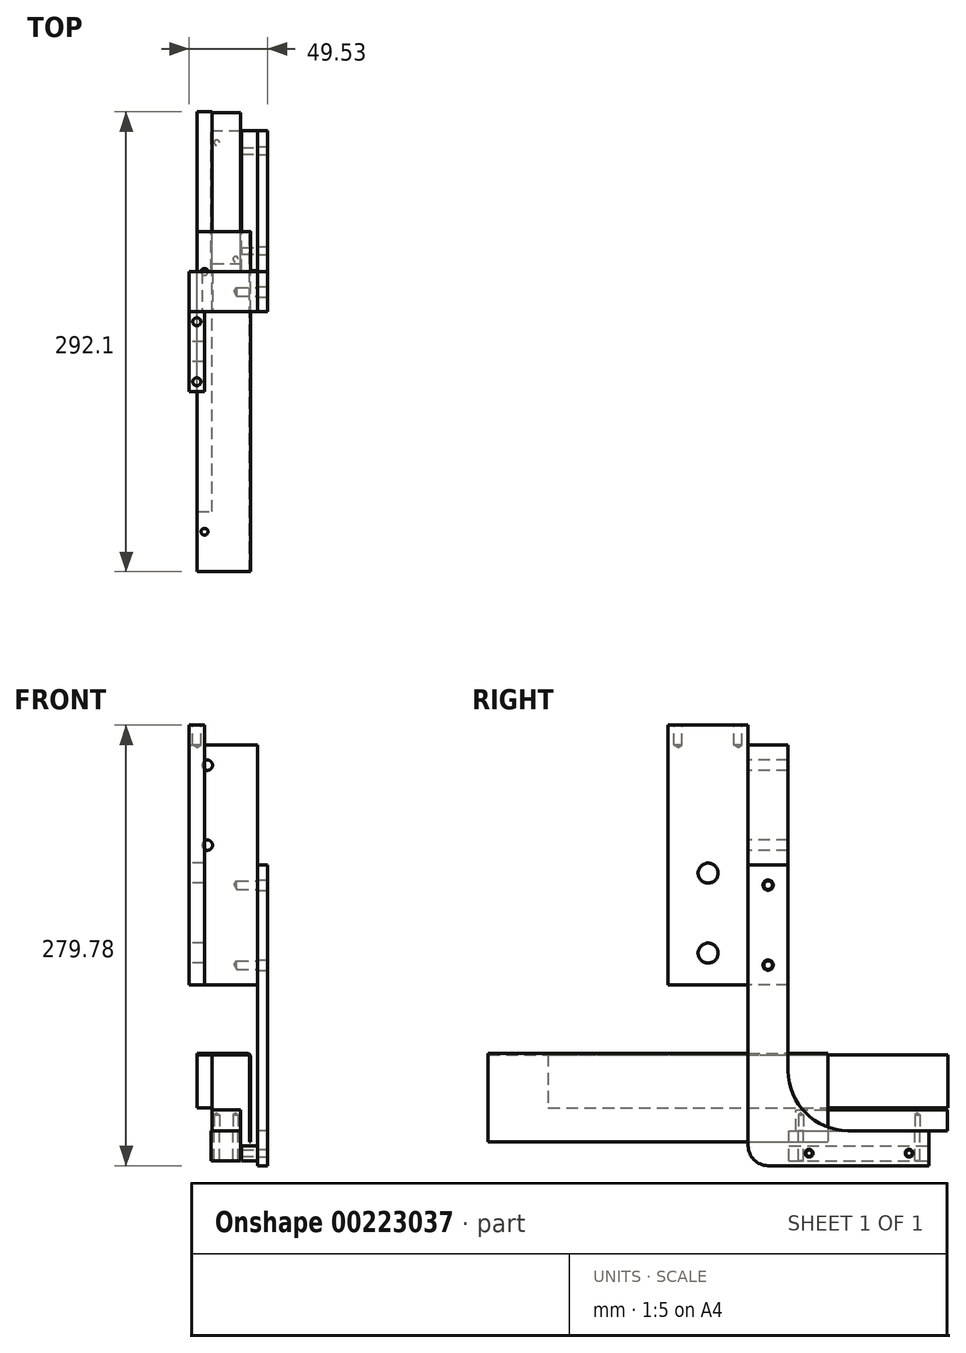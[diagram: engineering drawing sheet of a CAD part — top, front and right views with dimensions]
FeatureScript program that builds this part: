
annotation { "Feature Type Name" : "Feature", "Feature Type Description" : "" }
export const myFeature = defineFeature(function(context is Context, id is Id, definition is map)
    precondition{}
    {
        {
            var Q0;
            Q0=qCreatedBy(makeId("Front.planeOp"),FACE);
            var sketch = newSketch(context, id + "F0", { "sketchPlane" : qUnion([Q0])});
            skLineSegment(sketch, "E0.bottom", {"start": v(0, 0) * mm, "end": v(43.18, 0) * mm});
            skLineSegment(sketch, "E0.top", {"start": v(0, 152.4) * mm, "end": v(43.18, 152.4) * mm});
            skLineSegment(sketch, "E0.left", {"start": v(0, 0) * mm, "end": v(0, 152.4) * mm});
            skLineSegment(sketch, "E0.right", {"start": v(43.18, 0) * mm, "end": v(43.18, 152.4) * mm});
            skPoint(sketch, "E1", {"position": v(11.43, 139.7) * mm});
            skPoint(sketch, "E2", {"position": v(11.43, 88.9) * mm});
            skSolve(sketch);
        }
        {
            var Q0;
            Q0=makeQuery(id+"F0.imprint","IMPRINT",FACE,{"disambiguationData":[TD([[makeQuery(id+"F0.imprint","IMPRINT",EDGE,{"derivedFrom":sQuery(id+"F0.wireOp",EDGE,"E0.bottom")}),1.0]])]});
            extrude(context, id + "F1", {"entities" : qUnion([Q0]), "oppositeDirection" : true, "depth" : 25.4 * mm});
        }
        {
            var Q0;
            Q0=sQuery(id+"F0.wireOp",VERTEX,"E1");
            var Q1;
            Q1=sQuery(id+"F0.wireOp",VERTEX,"E2");
            var Q2;
            Q2=makeQuery(id+"F1.opExtrude","SWEPT_BODY",BODY,{"disambiguationData":[OSD([sQuery(id+"F0.wireOp",EDGE,"E0.bottom"),sQuery(id+"F0.wireOp",EDGE,"E0.top"),sQuery(id+"F0.wireOp",EDGE,"E0.left"),sQuery(id+"F0.wireOp",EDGE,"E0.right")])]});
            hole(context, id + "F2", {"style" : HoleStyle.SIMPLE, "endStyle" : HoleEndStyle.THROUGH, "standardTappedOrClearance" : lookupTablePath({ "standard" : "ANSI", "fit" : "Close", "size" : "1/4", "type" : "Clearance" }), "standardBlindInLast" : lookupTablePath({ "fit" : "Close", "standard" : "ANSI", "size" : "1/4", "type" : "Clearance" }), "holeDiameter" : 6.53 * mm, "locations" : qUnion([Q0, Q1]), "scope" : qUnion([Q2]), "isTappedThrough" : true});
        }
        {
            var Q0;
            Q0=qCreatedBy(makeId("Right.planeOp"),FACE);
            var sketch = newSketch(context, id + "F3", { "sketchPlane" : qUnion([Q0])});
            skLineSegment(sketch, "E3.bottom", {"start": v(0, 0) * mm, "end": v(-50.8, 0) * mm});
            skLineSegment(sketch, "E3.top", {"start": v(0, 165.1) * mm, "end": v(-50.8, 165.1) * mm});
            skLineSegment(sketch, "E3.left", {"start": v(0, 0) * mm, "end": v(0, 165.1) * mm});
            skLineSegment(sketch, "E3.right", {"start": v(-50.8, 0) * mm, "end": v(-50.8, 165.1) * mm});
            skPoint(sketch, "E4", {"position": v(-25.4, 71.12) * mm});
            skPoint(sketch, "E5", {"position": v(-25.4, 20.32) * mm});
            skSolve(sketch);
        }
        {
            var Q0;
            Q0=makeQuery(id+"F3.imprint","IMPRINT",FACE,{"disambiguationData":[TD([[makeQuery(id+"F3.imprint","IMPRINT",EDGE,{"derivedFrom":sQuery(id+"F3.wireOp",EDGE,"E3.bottom")}),-1.0]])]});
            extrude(context, id + "F4", {"entities" : qUnion([Q0]), "depth" : 9.52 * mm});
        }
        {
            var Q0;
            Q0=sQuery(id+"F3.wireOp",VERTEX,"E4");
            var Q1;
            Q1=sQuery(id+"F3.wireOp",VERTEX,"E5");
            var Q2;
            Q2=makeQuery(id+"F4.opExtrude","SWEPT_BODY",BODY,{"disambiguationData":[OSD([sQuery(id+"F3.wireOp",EDGE,"E3.bottom"),sQuery(id+"F3.wireOp",EDGE,"E3.top"),sQuery(id+"F3.wireOp",EDGE,"E3.left"),sQuery(id+"F3.wireOp",EDGE,"E3.right")])]});
            hole(context, id + "F5", {"style" : HoleStyle.SIMPLE, "endStyle" : HoleEndStyle.THROUGH, "oppositeDirection" : true, "holeDiameter" : 12.7 * mm, "locations" : qUnion([Q0, Q1]), "scope" : qUnion([Q2]), "isTappedThrough" : true});
        }
        {
            var Q0;
            Q0=makeQuery(id+"F4.opExtrude","SWEPT_FACE",FACE,{"disambiguationData":[OSD([sQuery(id+"F3.wireOp",EDGE,"E3.top")])]});
            var sketch = newSketch(context, id + "F6", { "sketchPlane" : qUnion([Q0])});
            skPoint(sketch, "E6", {"position": v(4.76, -6.35) * mm});
            skPoint(sketch, "E6.positionSnap0", {"position": v(4.76, 0) * mm});
            skPoint(sketch, "E7", {"position": v(4.76, -44.45) * mm});
            skSolve(sketch);
        }
        {
            var Q0;
            Q0=sQuery(id+"F6.wireOp",VERTEX,"E6");
            var Q1;
            Q1=sQuery(id+"F6.wireOp",VERTEX,"E7");
            var Q2;
            Q2=makeQuery(id+"F4.opExtrude","SWEPT_BODY",BODY,{"disambiguationData":[OSD([sQuery(id+"F3.wireOp",EDGE,"E3.bottom"),sQuery(id+"F3.wireOp",EDGE,"E3.top"),sQuery(id+"F3.wireOp",EDGE,"E3.left"),sQuery(id+"F3.wireOp",EDGE,"E3.right")])]});
            hole(context, id + "F7", {"style" : HoleStyle.SIMPLE, "endStyle" : HoleEndStyle.BLIND, "standardTappedOrClearance" : lookupTablePath({ "standard" : "ANSI", "engagement" : "75%", "pitch" : "20 tpi", "size" : "1/4", "type" : "Tapped" }), "standardBlindInLast" : lookupTablePath({ "standard" : "ANSI", "engagement" : "75%", "pitch" : "20 tpi", "size" : "1/4", "type" : "Tapped" }), "holeDiameter" : 5.1 * mm, "holeDepth" : 12.7 * mm, "locations" : qUnion([Q0, Q1]), "scope" : qUnion([Q2]), "majorDiameter" : 6.35 * mm});
        }
        {
            var Q0;
            Q0=qCreatedBy(makeId("Front.planeOp"),FACE);
            var sketch = newSketch(context, id + "F8", { "sketchPlane" : qUnion([Q0])});
            skLineSegment(sketch, "E8.bottom", {"start": v(4.9, -44.22) * mm, "end": v(14.43, -44.22) * mm});
            skLineSegment(sketch, "E8.top", {"start": v(4.9, -78.1) * mm, "end": v(14.43, -78.1) * mm});
            skLineSegment(sketch, "E8.left", {"start": v(4.9, -44.22) * mm, "end": v(4.9, -78.1) * mm});
            skLineSegment(sketch, "E8.right", {"start": v(14.43, -44.22) * mm, "end": v(14.43, -78.1) * mm});
            skSolve(sketch);
        }
        {
            var Q0;
            Q0=makeQuery(id+"F8.imprint","IMPRINT",FACE,{"disambiguationData":[TD([[makeQuery(id+"F8.imprint","IMPRINT",EDGE,{"derivedFrom":sQuery(id+"F8.wireOp",EDGE,"E8.bottom")}),-1.0]])]});
            extrude(context, id + "F9", {"entities" : qUnion([Q0]), "endBound" : BoundingType.SYMMETRIC, "depth" : 254 * mm});
        }
        {
            var Q0;
            Q0=makeQuery(id+"F9.opExtrude","SWEPT_FACE",FACE,{"disambiguationData":[OSD([sQuery(id+"F8.wireOp",EDGE,"E8.top")])]});
            cPlane(context, id + "F10", {"entities" : qUnion([Q0]), "cplaneType" : CPlaneType.OFFSET, "offset" : 1.02 * mm, "width" : 152.4 * mm, "height" : 152.4 * mm});
        }
        {
            var Q0;
            Q0=qCreatedBy(id+"F10.planeOp",FACE);
            var sketch = newSketch(context, id + "F11", { "sketchPlane" : qUnion([Q0])});
            skLineSegment(sketch, "E9.0", {"start": v(14.43, 127) * mm, "end": v(14.43, -127) * mm});
            skLineSegment(sketch, "E10.bottom", {"start": v(14.43, -30.48) * mm, "end": v(32.44, -30.48) * mm});
            skLineSegment(sketch, "E10.top", {"start": v(14.43, -126.48) * mm, "end": v(32.44, -126.48) * mm});
            skLineSegment(sketch, "E10.left", {"start": v(14.43, -30.48) * mm, "end": v(14.43, -126.48) * mm});
            skLineSegment(sketch, "E10.right", {"start": v(32.44, -30.48) * mm, "end": v(32.44, -126.48) * mm});
            skPoint(sketch, "E11", {"position": v(29.44, -33.48) * mm});
            skPoint(sketch, "E12", {"position": v(17.44, -107.48) * mm});
            skSolve(sketch);
        }
        {
            var Q0;
            Q0=makeQuery(id+"F11.imprint","IMPRINT",FACE,{"disambiguationData":[TD([[makeQuery(id+"F11.imprint","IMPRINT",EDGE,{"derivedFrom":sQuery(id+"F11.wireOp",EDGE,"E10.bottom")}),-1.0]])]});
            extrude(context, id + "F12", {"entities" : qUnion([Q0]), "depth" : 13.33 * mm});
        }
        {
            var Q0;
            Q0=makeQuery(id+"F12.opExtrude","CAP_FACE",FACE,{"disambiguationData":[OSD([sQuery(id+"F11.wireOp",EDGE,"E10.bottom"),sQuery(id+"F11.wireOp",EDGE,"E10.top"),sQuery(id+"F11.wireOp",EDGE,"E10.left"),sQuery(id+"F11.wireOp",EDGE,"E10.right")])],"isStart":false});
            var sketch = newSketch(context, id + "F13", { "sketchPlane" : qUnion([Q0])});
            skLineSegment(sketch, "E13.0.0", {"start": v(32.44, -30.48) * mm, "end": v(14.43, -30.48) * mm});
            skLineSegment(sketch, "E13.0.1", {"start": v(14.43, -30.48) * mm, "end": v(14.43, -126.48) * mm});
            skLineSegment(sketch, "E13.0.2", {"start": v(14.43, -126.48) * mm, "end": v(32.44, -126.48) * mm});
            skLineSegment(sketch, "E13.0.3", {"start": v(32.44, -126.48) * mm, "end": v(32.44, -30.48) * mm});
            skPoint(sketch, "E14.0", {"position": v(29.44, -33.48) * mm});
            skPoint(sketch, "E15.0", {"position": v(17.44, -107.48) * mm});
            skSolve(sketch);
        }
        {
            var Q0;
            Q0=sQuery(id+"F13.wireOp",VERTEX,"E14.0");
            var Q1;
            Q1=sQuery(id+"F13.wireOp",VERTEX,"E15.0");
            var Q2;
            Q2=makeQuery(id+"F12.opExtrude","SWEPT_BODY",BODY,{"disambiguationData":[OSD([sQuery(id+"F11.wireOp",EDGE,"E10.bottom"),sQuery(id+"F11.wireOp",EDGE,"E10.top"),sQuery(id+"F11.wireOp",EDGE,"E10.left"),sQuery(id+"F11.wireOp",EDGE,"E10.right")])]});
            hole(context, id + "F14", {"style" : HoleStyle.SIMPLE, "endStyle" : HoleEndStyle.BLIND, "standardTappedOrClearance" : lookupTablePath({ "standard" : "ISO", "engagement" : "75%", "pitch" : "0.7 mm", "size" : "M4", "type" : "Tapped" }), "standardBlindInLast" : lookupTablePath({ "standard" : "ISO", "engagement" : "75%", "pitch" : "0.7 mm", "size" : "M4", "type" : "Tapped" }), "holeDiameter" : 3.3 * mm, "showTappedDepth" : true, "holeDepth" : 10.16 * mm, "tappedDepth" : 8.06 * mm, "tapClearance" : 3, "locations" : qUnion([Q0, Q1]), "scope" : qUnion([Q2]), "majorDiameter" : 4 * mm});
        }
        {
            var Q0;
            Q0=makeQuery(id+"F12.opExtrude","CAP_FACE",FACE,{"disambiguationData":[OSD([sQuery(id+"F11.wireOp",EDGE,"E10.bottom"),sQuery(id+"F11.wireOp",EDGE,"E10.top"),sQuery(id+"F11.wireOp",EDGE,"E10.left"),sQuery(id+"F11.wireOp",EDGE,"E10.right")])],"isStart":false});
            var sketch = newSketch(context, id + "F15", { "sketchPlane" : qUnion([Q0])});
            skLineSegment(sketch, "E16.bottom", {"start": v(14.43, -26.04) * mm, "end": v(43.18, -26.04) * mm});
            skLineSegment(sketch, "E16.top", {"start": v(14.43, -114.94) * mm, "end": v(43.18, -114.94) * mm});
            skLineSegment(sketch, "E16.left", {"start": v(14.43, -26.04) * mm, "end": v(14.43, -114.94) * mm});
            skLineSegment(sketch, "E16.right", {"start": v(43.18, -26.04) * mm, "end": v(43.18, -114.94) * mm});
            skLineSegment(sketch, "E17", {"start": v(32.44, -30.48) * mm, "end": v(32.44, -26.04) * mm});
            skLineSegment(sketch, "E18.bottom", {"start": v(14.43, -26.04) * mm, "end": v(13.67, -26.04) * mm});
            skLineSegment(sketch, "E18.top", {"start": v(14.43, -114.94) * mm, "end": v(13.67, -114.94) * mm});
            skLineSegment(sketch, "E18.right", {"start": v(13.67, -26.04) * mm, "end": v(13.67, -114.94) * mm});
            skLineSegment(sketch, "E19.bottom", {"start": v(32.44, -26.04) * mm, "end": v(33.2, -26.04) * mm});
            skLineSegment(sketch, "E19.top", {"start": v(32.44, -114.94) * mm, "end": v(33.2, -114.94) * mm});
            skLineSegment(sketch, "E19.left", {"start": v(32.44, -26.04) * mm, "end": v(32.44, -114.94) * mm});
            skLineSegment(sketch, "E19.right", {"start": v(33.2, -26.04) * mm, "end": v(33.2, -114.94) * mm});
            skSolve(sketch);
        }
        {
            var Q0;
            {var subQ0=makeQuery(id+"F12.opExtrude","CAP_EDGE",EDGE,{"disambiguationData":[OSD([sQuery(id+"F11.wireOp",EDGE,"E10.bottom")])],"isStart":false});Q0=makeQuery(id+"F15.imprint","IMPRINT",FACE,{"disambiguationData":[TD([[makeQuery(id+"F15.imprint","IMPRINT",EDGE,{"derivedFrom":subQ0}),-1.0]])]});}
            var Q1;
            {var subQ3=sQuery(id+"F15.wireOp",EDGE,"E17");Q1=makeQuery(id+"F15.imprint","IMPRINT",FACE,{"disambiguationData":[TD([[makeQuery(id+"F15.imprint","IMPRINT",EDGE,{"derivedFrom":subQ3}),1.0]])]});}
            var Q2;
            Q2=makeQuery(id+"F15.imprint","IMPRINT",FACE,{"disambiguationData":[TD([[makeQuery(id+"F15.imprint","IMPRINT",EDGE,{"derivedFrom":makeQuery(id+"F14.hole-0.boolean.opBoolean","COPY",EDGE,{"derivedFrom":makeQuery(id+"F14.hole-0.opRevolve","SWEPT_EDGE",EDGE,{"disambiguationData":[OSD([sQuery(id+"F14.hole-0.sketch.wireOp",EDGE,"core_line_2"),sQuery(id+"F14.hole-0.sketch.wireOp",EDGE,"core_line_3")])]})})}),1.0]])]});
            var Q3;
            Q3=makeQuery(id+"F15.imprint","IMPRINT",FACE,{"disambiguationData":[TD([[makeQuery(id+"F15.imprint","IMPRINT",EDGE,{"derivedFrom":makeQuery(id+"F14.hole-1.boolean.opBoolean","COPY",EDGE,{"derivedFrom":makeQuery(id+"F14.hole-1.opRevolve","SWEPT_EDGE",EDGE,{"disambiguationData":[OSD([sQuery(id+"F14.hole-1.sketch.wireOp",EDGE,"core_line_2"),sQuery(id+"F14.hole-1.sketch.wireOp",EDGE,"core_line_3")])]})})}),1.0]])]});
            var Q4;
            {var subQ1=sQuery(id+"F15.wireOp",EDGE,"E16.right");Q4=makeQuery(id+"F15.imprint","IMPRINT",FACE,{"disambiguationData":[TD([[makeQuery(id+"F15.imprint","IMPRINT",EDGE,{"derivedFrom":subQ1}),-1.0]])]});}
            var Q5;
            {var subQ2=sQuery(id+"F15.wireOp",EDGE,"E18.bottom");Q5=makeQuery(id+"F15.imprint","IMPRINT",FACE,{"disambiguationData":[TD([[makeQuery(id+"F15.imprint","IMPRINT",EDGE,{"derivedFrom":subQ2}),1.0]])]});}
            var Q6;
            {var subQ2=sQuery(id+"F15.wireOp",EDGE,"E19.bottom");Q6=makeQuery(id+"F15.imprint","IMPRINT",FACE,{"disambiguationData":[TD([[makeQuery(id+"F15.imprint","IMPRINT",EDGE,{"derivedFrom":subQ2}),-1.0]])]});}
            var Q7;
            {var subQ5=makeQuery(id+"F12.opExtrude","CAP_EDGE",EDGE,{"disambiguationData":[OSD([sQuery(id+"F11.wireOp",EDGE,"E10.bottom")])],"isStart":false});Q7=makeQuery(id+"F15.imprint","IMPRINT",FACE,{"disambiguationData":[TD([[makeQuery(id+"F15.imprint","IMPRINT",EDGE,{"derivedFrom":subQ5}),1.0]])]});}
            extrude(context, id + "F16", {"entities" : qUnion([Q0, Q1, Q2, Q3, Q4, Q5, Q6, Q7]), "depth" : 19.05 * mm});
        }
        {
            var Q0;
            {var subQ1=sQuery(id+"F15.wireOp",EDGE,"E16.right");Q0=makeQuery(id+"F15.imprint","IMPRINT",FACE,{"disambiguationData":[TD([[makeQuery(id+"F15.imprint","IMPRINT",EDGE,{"derivedFrom":subQ1}),-1.0]])]});}
            extrude(context, id + "F17", {"entities" : qUnion([Q0]), "operationType" : NewBodyOperationType.REMOVE, "depth" : 9.52 * mm});
        }
        {
            var Q0;
            Q0=sQuery(id+"F13.wireOp",VERTEX,"E14.0");
            var Q1;
            Q1=sQuery(id+"F13.wireOp",VERTEX,"E15.0");
            var Q2;
            Q2=makeQuery(id+"F16.opExtrude","SWEPT_BODY",BODY,{"disambiguationData":[OSD([sQuery(id+"F15.wireOp",EDGE,"E16.bottom"),sQuery(id+"F15.wireOp",EDGE,"E16.top"),sQuery(id+"F15.wireOp",EDGE,"E16.left"),sQuery(id+"F15.wireOp",EDGE,"E16.right")])]});
            hole(context, id + "F18", {"style" : HoleStyle.SIMPLE, "endStyle" : HoleEndStyle.THROUGH, "oppositeDirection" : true, "standardTappedOrClearance" : lookupTablePath({ "standard" : "ISO", "fit" : "Normal", "size" : "M4", "type" : "Clearance" }), "standardBlindInLast" : lookupTablePath({ "fit" : "Standard", "standard" : "ISO", "size" : "M4", "type" : "Clearance" }), "holeDiameter" : 4.4 * mm, "tappedDepth" : 8.06 * mm, "tapClearance" : 3, "locations" : qUnion([Q0, Q1]), "scope" : qUnion([Q2])});
        }
        {
            var Q0;
            Q0=makeQuery(id+"F16.opExtrude","SWEPT_FACE",FACE,{"disambiguationData":[OSD([sQuery(id+"F15.wireOp",EDGE,"E16.right")])]});
            var sketch = newSketch(context, id + "F19", { "sketchPlane" : qUnion([Q0])});
            skPoint(sketch, "E20", {"position": v(38.74, -106.74) * mm});
            skPoint(sketch, "E20.positionSnap0", {"position": v(26.04, -106.74) * mm});
            skPoint(sketch, "E21", {"position": v(102.23, -106.74) * mm});
            skSolve(sketch);
        }
        {
            var Q0;
            Q0=sQuery(id+"F19.wireOp",VERTEX,"E20");
            var Q1;
            Q1=sQuery(id+"F19.wireOp",VERTEX,"E21");
            var Q2;
            Q2=makeQuery(id+"F16.opExtrude","SWEPT_BODY",BODY,{"disambiguationData":[OSD([sQuery(id+"F15.wireOp",EDGE,"E16.bottom"),sQuery(id+"F15.wireOp",EDGE,"E16.top"),sQuery(id+"F15.wireOp",EDGE,"E16.right"),sQuery(id+"F15.wireOp",EDGE,"E18.bottom"),sQuery(id+"F15.wireOp",EDGE,"E18.top"),sQuery(id+"F15.wireOp",EDGE,"E18.right"),sQuery(id+"F15.wireOp",EDGE,"E19.bottom"),sQuery(id+"F15.wireOp",EDGE,"E19.top")])]});
            hole(context, id + "F20", {"style" : HoleStyle.SIMPLE, "endStyle" : HoleEndStyle.BLIND, "standardTappedOrClearance" : lookupTablePath({ "standard" : "ANSI", "engagement" : "75%", "pitch" : "32 tpi", "size" : "#10", "type" : "Tapped" }), "standardBlindInLast" : lookupTablePath({ "standard" : "ANSI", "engagement" : "75%", "pitch" : "32 tpi", "size" : "#10", "type" : "Tapped" }), "holeDiameter" : 4.04 * mm, "showTappedDepth" : true, "holeDepth" : 12.7 * mm, "tappedDepth" : 10.32 * mm, "tapClearance" : 3, "locations" : qUnion([Q0, Q1]), "scope" : qUnion([Q2]), "majorDiameter" : 4.83 * mm});
        }
        {
            var Q0;
            Q0=makeQuery(id+"F1.opExtrude","SWEPT_FACE",FACE,{"disambiguationData":[OSD([sQuery(id+"F0.wireOp",EDGE,"E0.right")])]});
            var sketch = newSketch(context, id + "F21", { "sketchPlane" : qUnion([Q0])});
            skPoint(sketch, "E22", {"position": v(12.7, 12.7) * mm});
            skPoint(sketch, "E22.positionSnap0", {"position": v(12.7, 0) * mm});
            skPoint(sketch, "E23", {"position": v(12.7, 63.5) * mm});
            skSolve(sketch);
        }
        {
            var Q0;
            Q0=sQuery(id+"F21.wireOp",VERTEX,"E23");
            var Q1;
            Q1=sQuery(id+"F21.wireOp",VERTEX,"E22");
            var Q2;
            Q2=makeQuery(id+"F1.opExtrude","SWEPT_BODY",BODY,{"disambiguationData":[OSD([sQuery(id+"F0.wireOp",EDGE,"E0.bottom"),sQuery(id+"F0.wireOp",EDGE,"E0.top"),sQuery(id+"F0.wireOp",EDGE,"E0.left"),sQuery(id+"F0.wireOp",EDGE,"E0.right")])]});
            hole(context, id + "F22", {"style" : HoleStyle.SIMPLE, "endStyle" : HoleEndStyle.BLIND, "standardTappedOrClearance" : lookupTablePath({ "standard" : "ANSI", "engagement" : "75%", "pitch" : "28 tpi", "size" : "1/4", "type" : "Tapped" }), "standardBlindInLast" : lookupTablePath({ "standard" : "ANSI", "engagement" : "75%", "pitch" : "28 tpi", "size" : "1/4", "type" : "Tapped" }), "holeDiameter" : 5.4 * mm, "showTappedDepth" : true, "holeDepth" : 13.04 * mm, "tappedDepth" : 10.32 * mm, "tapClearance" : 3, "locations" : qUnion([Q0, Q1]), "scope" : qUnion([Q2]), "majorDiameter" : 6.35 * mm});
        }
        {
            var Q0;
            Q0=makeQuery(id+"F1.opExtrude","SWEPT_FACE",FACE,{"disambiguationData":[OSD([sQuery(id+"F0.wireOp",EDGE,"E0.right")])]});
            var sketch = newSketch(context, id + "F23", { "sketchPlane" : qUnion([Q0])});
            skLineSegment(sketch, "E24.0.0", {"start": v(114.94, -101.98) * mm, "end": v(26.04, -101.98) * mm});
            skLineSegment(sketch, "E24.0.1", {"start": v(26.04, -101.98) * mm, "end": v(26.04, -111.5) * mm});
            skLineSegment(sketch, "E24.0.2", {"start": v(26.04, -111.5) * mm, "end": v(114.94, -111.5) * mm});
            skLineSegment(sketch, "E24.0.3", {"start": v(114.94, -111.5) * mm, "end": v(114.94, -101.98) * mm});
            skLineSegment(sketch, "E25.bottom", {"start": v(0, 76.2) * mm, "end": v(25.4, 76.2) * mm});
            skLineSegment(sketch, "E25.top", {"start": v(0, -111.5) * mm, "end": v(114.94, -111.5) * mm});
            skLineSegment(sketch, "E25.left", {"start": v(0, 76.2) * mm, "end": v(0, -111.5) * mm});
            skLineSegment(sketch, "E25.right", {"start": v(114.94, -101.98) * mm, "end": v(114.94, -111.5) * mm});
            skLineSegment(sketch, "E26", {"start": v(25.4, 76.2) * mm, "end": v(25.4, -101.98) * mm});
            skLineSegment(sketch, "E27", {"start": v(25.4, -101.98) * mm, "end": v(114.94, -101.98) * mm});
            skCircle(sketch, "E28", {"center": v(63.5, -54.36) * mm, "radius": 38.1 * mm});
            skLineSegment(sketch, "E29", {"start": v(114.94, -101.98) * mm, "end": v(114.94, -92.46) * mm});
            skLineSegment(sketch, "E30", {"start": v(114.94, -92.46) * mm, "end": v(25.4, -92.46) * mm});
            skLineSegment(sketch, "E31.top", {"start": v(0, -114.68) * mm, "end": v(114.94, -114.68) * mm});
            skLineSegment(sketch, "E31.left", {"start": v(0, -111.5) * mm, "end": v(0, -114.68) * mm});
            skLineSegment(sketch, "E31.right", {"start": v(114.94, -111.5) * mm, "end": v(114.94, -114.68) * mm});
            skSolve(sketch);
        }
        {
            var Q0;
            {var subQ3=sQuery(id+"F23.wireOp",EDGE,"E25.bottom");Q0=makeQuery(id+"F23.imprint","IMPRINT",FACE,{"disambiguationData":[TD([[makeQuery(id+"F23.imprint","IMPRINT",EDGE,{"derivedFrom":subQ3}),-1.0]])]});}
            var Q1;
            {var subQ6=sQuery(id+"F23.wireOp",EDGE,"E24.0.1");Q1=makeQuery(id+"F23.imprint","IMPRINT",FACE,{"disambiguationData":[TD([[makeQuery(id+"F23.imprint","IMPRINT",EDGE,{"derivedFrom":subQ6}),-1.0]])]});}
            var Q2;
            {var subQ2=sQuery(id+"F23.wireOp",EDGE,"E29");Q2=makeQuery(id+"F23.imprint","IMPRINT",FACE,{"disambiguationData":[TD([[makeQuery(id+"F23.imprint","IMPRINT",EDGE,{"derivedFrom":subQ2}),1.0]])]});}
            var Q3;
            {var subQ0=sQuery(id+"F23.wireOp",EDGE,"E24.0.1");Q3=makeQuery(id+"F23.imprint","IMPRINT",FACE,{"disambiguationData":[TD([[makeQuery(id+"F23.imprint","IMPRINT",EDGE,{"derivedFrom":subQ0}),1.0]])]});}
            var Q4;
            {var subQ0=sQuery(id+"F23.wireOp",EDGE,"E30");var subQ1=sQuery(id+"F23.wireOp",EDGE,"E26");var subQ2=makeQuery(id+"F23.imprint","INTERSECT",VERTEX,{"derivedFrom":[subQ1,subQ0]});Q4=makeQuery(id+"F23.imprint","IMPRINT",FACE,{"disambiguationData":[TD([[makeQuery(id+"F23.imprint","IMPRINT",EDGE,{"disambiguationData":[TD([[subQ2,1.0]])],"derivedFrom":subQ1}),1.0]])]});}
            var Q5;
            Q5=makeQuery(id+"F23.imprint","IMPRINT",FACE,{"disambiguationData":[TD([[makeQuery(id+"F23.imprint","IMPRINT",EDGE,{"derivedFrom":makeQuery(id+"F22.hole-0.boolean.opBoolean","COPY",EDGE,{"derivedFrom":makeQuery(id+"F22.hole-0.opRevolve","SWEPT_EDGE",EDGE,{"disambiguationData":[OSD([sQuery(id+"F22.hole-0.sketch.wireOp",EDGE,"core_line_2"),sQuery(id+"F22.hole-0.sketch.wireOp",EDGE,"core_line_3")])]})})}),1.0]])]});
            var Q6;
            Q6=makeQuery(id+"F23.imprint","IMPRINT",FACE,{"disambiguationData":[TD([[makeQuery(id+"F23.imprint","IMPRINT",EDGE,{"derivedFrom":makeQuery(id+"F22.hole-1.boolean.opBoolean","COPY",EDGE,{"derivedFrom":makeQuery(id+"F22.hole-1.opRevolve","SWEPT_EDGE",EDGE,{"disambiguationData":[OSD([sQuery(id+"F22.hole-1.sketch.wireOp",EDGE,"core_line_2"),sQuery(id+"F22.hole-1.sketch.wireOp",EDGE,"core_line_3")])]})})}),1.0]])]});
            var Q7;
            Q7=makeQuery(id+"F23.imprint","IMPRINT",FACE,{"disambiguationData":[TD([[makeQuery(id+"F23.imprint","IMPRINT",EDGE,{"derivedFrom":sQuery(id+"F23.wireOp",EDGE,"E31.top")}),1.0]])]});
            extrude(context, id + "F24", {"entities" : qUnion([Q0, Q1, Q2, Q3, Q4, Q5, Q6, Q7]), "depth" : 6.35 * mm});
        }
        {
            var Q0;
            Q0=makeQuery(id+"F24.opExtrude","CAP_FACE",FACE,{"disambiguationData":[OSD([sQuery(id+"F23.wireOp",EDGE,"E25.bottom"),sQuery(id+"F23.wireOp",EDGE,"E25.top"),sQuery(id+"F23.wireOp",EDGE,"E25.left"),sQuery(id+"F23.wireOp",EDGE,"E25.right"),sQuery(id+"F23.wireOp",EDGE,"E26"),sQuery(id+"F23.wireOp",EDGE,"E28"),sQuery(id+"F23.wireOp",EDGE,"E29"),sQuery(id+"F23.wireOp",EDGE,"E30")])],"isStart":false});
            var sketch = newSketch(context, id + "F25", { "sketchPlane" : qUnion([Q0])});
            skLineSegment(sketch, "E32.0.0", {"start": v(0, 152.4) * mm, "end": v(0, 0) * mm});
            skLineSegment(sketch, "E32.0.1", {"start": v(0, 0) * mm, "end": v(25.4, 0) * mm});
            skLineSegment(sketch, "E32.0.2", {"start": v(25.4, 0) * mm, "end": v(25.4, 152.4) * mm});
            skLineSegment(sketch, "E32.0.3", {"start": v(25.4, 152.4) * mm, "end": v(0, 152.4) * mm});
            skCircle(sketch, "E33.0", {"center": v(102.23, -106.74) * mm, "radius": 2.02 * mm});
            skCircle(sketch, "E34.0", {"center": v(38.74, -106.74) * mm, "radius": 2.02 * mm});
            skCircle(sketch, "E35.0", {"center": v(12.7, 12.7) * mm, "radius": 2.7 * mm});
            skCircle(sketch, "E36.0", {"center": v(12.7, 63.5) * mm, "radius": 2.7 * mm});
            skSolve(sketch);
        }
        {
            var Q0;
            Q0=sQuery(id+"F25.wireOp",VERTEX,"E36.0.center");
            var Q1;
            Q1=sQuery(id+"F25.wireOp",VERTEX,"E35.0.center");
            var Q2;
            Q2=makeQuery(id+"F24.opExtrude","SWEPT_BODY",BODY,{"disambiguationData":[OSD([sQuery(id+"F23.wireOp",EDGE,"E25.bottom"),sQuery(id+"F23.wireOp",EDGE,"E25.top"),sQuery(id+"F23.wireOp",EDGE,"E25.left"),sQuery(id+"F23.wireOp",EDGE,"E25.right"),sQuery(id+"F23.wireOp",EDGE,"E26"),sQuery(id+"F23.wireOp",EDGE,"E28"),sQuery(id+"F23.wireOp",EDGE,"E29"),sQuery(id+"F23.wireOp",EDGE,"E30")])]});
            hole(context, id + "F26", {"style" : HoleStyle.SIMPLE, "endStyle" : HoleEndStyle.THROUGH, "standardTappedOrClearance" : lookupTablePath({ "standard" : "ANSI", "fit" : "Close", "size" : "1/4", "type" : "Clearance" }), "standardBlindInLast" : lookupTablePath({ "fit" : "Close", "standard" : "ANSI", "size" : "1/4", "type" : "Clearance" }), "holeDiameter" : 6.53 * mm, "tappedDepth" : 10.3 * mm, "tapClearance" : 3, "locations" : qUnion([Q0, Q1]), "scope" : qUnion([Q2])});
        }
        {
            var Q0;
            Q0=sQuery(id+"F25.wireOp",VERTEX,"E34.0.center");
            var Q1;
            Q1=sQuery(id+"F25.wireOp",VERTEX,"E33.0.center");
            var Q2;
            Q2=makeQuery(id+"F24.opExtrude","SWEPT_BODY",BODY,{"disambiguationData":[OSD([sQuery(id+"F23.wireOp",EDGE,"E25.bottom"),sQuery(id+"F23.wireOp",EDGE,"E25.top"),sQuery(id+"F23.wireOp",EDGE,"E25.left"),sQuery(id+"F23.wireOp",EDGE,"E25.right"),sQuery(id+"F23.wireOp",EDGE,"E26"),sQuery(id+"F23.wireOp",EDGE,"E28"),sQuery(id+"F23.wireOp",EDGE,"E29"),sQuery(id+"F23.wireOp",EDGE,"E30")])]});
            hole(context, id + "F27", {"style" : HoleStyle.SIMPLE, "endStyle" : HoleEndStyle.THROUGH, "standardTappedOrClearance" : lookupTablePath({ "standard" : "ANSI", "fit" : "Close", "size" : "#10", "type" : "Clearance" }), "standardBlindInLast" : lookupTablePath({ "fit" : "Close", "standard" : "ANSI", "size" : "#10", "type" : "Clearance" }), "holeDiameter" : 4.98 * mm, "tappedDepth" : 10.3 * mm, "tapClearance" : 3, "locations" : qUnion([Q0, Q1]), "scope" : qUnion([Q2])});
        }
        {
            var Q0;
            Q0=makeQuery(id+"F24.opExtrude","SWEPT_EDGE",EDGE,{"disambiguationData":[OSD([sQuery(id+"F23.wireOp",EDGE,"E31.top"),sQuery(id+"F23.wireOp",EDGE,"E31.left")])]});
            fillet(context, id + "F28", {"entities" : qUnion([Q0]), "radius" : 12.7 * mm, "tangentPropagation" : true, "allowEdgeOverflow" : false});
        }
        {
            var Q0;
            Q0=qCreatedBy(makeId("Front.planeOp"),FACE);
            cPlane(context, id + "F29", {"entities" : qUnion([Q0]), "cplaneType" : CPlaneType.OFFSET, "offset" : 50.8 * mm, "oppositeDirection" : true, "width" : 152.4 * mm, "height" : 152.4 * mm});
        }
        {
            var Q0;
            Q0=qCreatedBy(id+"F29.planeOp",FACE);
            var sketch = newSketch(context, id + "F30", { "sketchPlane" : qUnion([Q0])});
            skLineSegment(sketch, "E37.0.0", {"start": v(4.9, -78.1) * mm, "end": v(4.9, -44.22) * mm});
            skLineSegment(sketch, "E37.0.1", {"start": v(4.9, -44.22) * mm, "end": v(14.43, -44.22) * mm});
            skLineSegment(sketch, "E37.0.2", {"start": v(14.43, -44.22) * mm, "end": v(14.43, -78.1) * mm});
            skLineSegment(sketch, "E37.0.3", {"start": v(14.43, -78.1) * mm, "end": v(4.9, -78.1) * mm});
            skLineSegment(sketch, "E38.0.0", {"start": v(33.2, -92.46) * mm, "end": v(33.2, -101.98) * mm});
            skLineSegment(sketch, "E38.0.1", {"start": v(33.2, -101.98) * mm, "end": v(43.18, -101.98) * mm});
            skLineSegment(sketch, "E38.0.2", {"start": v(43.18, -101.98) * mm, "end": v(43.18, -111.5) * mm});
            skLineSegment(sketch, "E38.0.3", {"start": v(43.18, -111.5) * mm, "end": v(13.67, -111.5) * mm});
            skLineSegment(sketch, "E38.0.4", {"start": v(13.67, -111.5) * mm, "end": v(13.67, -92.46) * mm});
            skLineSegment(sketch, "E38.0.5", {"start": v(13.67, -92.46) * mm, "end": v(33.2, -92.46) * mm});
            skLineSegment(sketch, "E39", {"start": v(4.9, -44.22) * mm, "end": v(36.61, -44.22) * mm});
            skPoint(sketch, "E39.endSnap0", {"position": v(38.19, -101.98) * mm});
            skLineSegment(sketch, "E40", {"start": v(38.19, -45.8) * mm, "end": v(38.19, -99.44) * mm});
            skPoint(sketch, "E41.visualSharp", {"position": v(38.19, -44.22) * mm});
            skArc(sketch, "E41.filletArc", {"start": v(38.19, -45.8) * mm, "mid": v(37.73, -44.68) * mm, "end": v(36.61, -44.22) * mm});
            skLineSegment(sketch, "E42.0", {"start": v(39, -45.8) * mm, "end": v(39, -99.44) * mm});
            skLineSegment(sketch, "E43.0", {"start": v(4.9, -43.4) * mm, "end": v(36.61, -43.4) * mm});
            skArc(sketch, "E44.0", {"start": v(39, -45.8) * mm, "mid": v(38.3, -44.1) * mm, "end": v(36.61, -43.4) * mm});
            skLineSegment(sketch, "E45", {"start": v(4.9, -43.4) * mm, "end": v(4.9, -44.22) * mm});
            skLineSegment(sketch, "E46", {"start": v(39, -99.44) * mm, "end": v(38.19, -99.44) * mm});
            skSolve(sketch);
        }
        {
            var Q0;
            Q0=makeQuery(id+"F30.imprint","IMPRINT",FACE,{"disambiguationData":[TD([[makeQuery(id+"F30.imprint","IMPRINT",EDGE,{"derivedFrom":sQuery(id+"F30.wireOp",EDGE,"E40")}),1.0]])]});
            extrude(context, id + "F31", {"entities" : qUnion([Q0]), "depth" : 215.9 * mm});
        }
        {
            var Q0;
            Q0=makeQuery(id+"F31.opExtrude","SWEPT_FACE",FACE,{"disambiguationData":[OSD([sQuery(id+"F30.wireOp",EDGE,"E43.0")])]});
            var sketch = newSketch(context, id + "F32", { "sketchPlane" : qUnion([Q0])});
            skPoint(sketch, "E47", {"position": v(9.66, -139.7) * mm});
            skPoint(sketch, "E48", {"position": v(9.66, 25.4) * mm});
            skSolve(sketch);
        }
        {
            var Q0;
            Q0=sQuery(id+"F32.wireOp",VERTEX,"E47");
            var Q1;
            Q1=sQuery(id+"F32.wireOp",VERTEX,"E48");
            var Q2;
            Q2=makeQuery(id+"F31.opExtrude","SWEPT_BODY",BODY,{"disambiguationData":[OSD([sQuery(id+"F30.wireOp",EDGE,"E39"),sQuery(id+"F30.wireOp",EDGE,"E40"),sQuery(id+"F30.wireOp",EDGE,"E41.filletArc"),sQuery(id+"F30.wireOp",EDGE,"E42.0"),sQuery(id+"F30.wireOp",EDGE,"E43.0"),sQuery(id+"F30.wireOp",EDGE,"E44.0"),sQuery(id+"F30.wireOp",EDGE,"E45"),sQuery(id+"F30.wireOp",EDGE,"E46")])]});
            hole(context, id + "F33", {"style" : HoleStyle.SIMPLE, "endStyle" : HoleEndStyle.THROUGH, "holeDiameter" : 4.32 * mm, "tappedDepth" : 10.3 * mm, "tapClearance" : 3, "locations" : qUnion([Q0, Q1]), "scope" : qUnion([Q2])});
        }
    });
